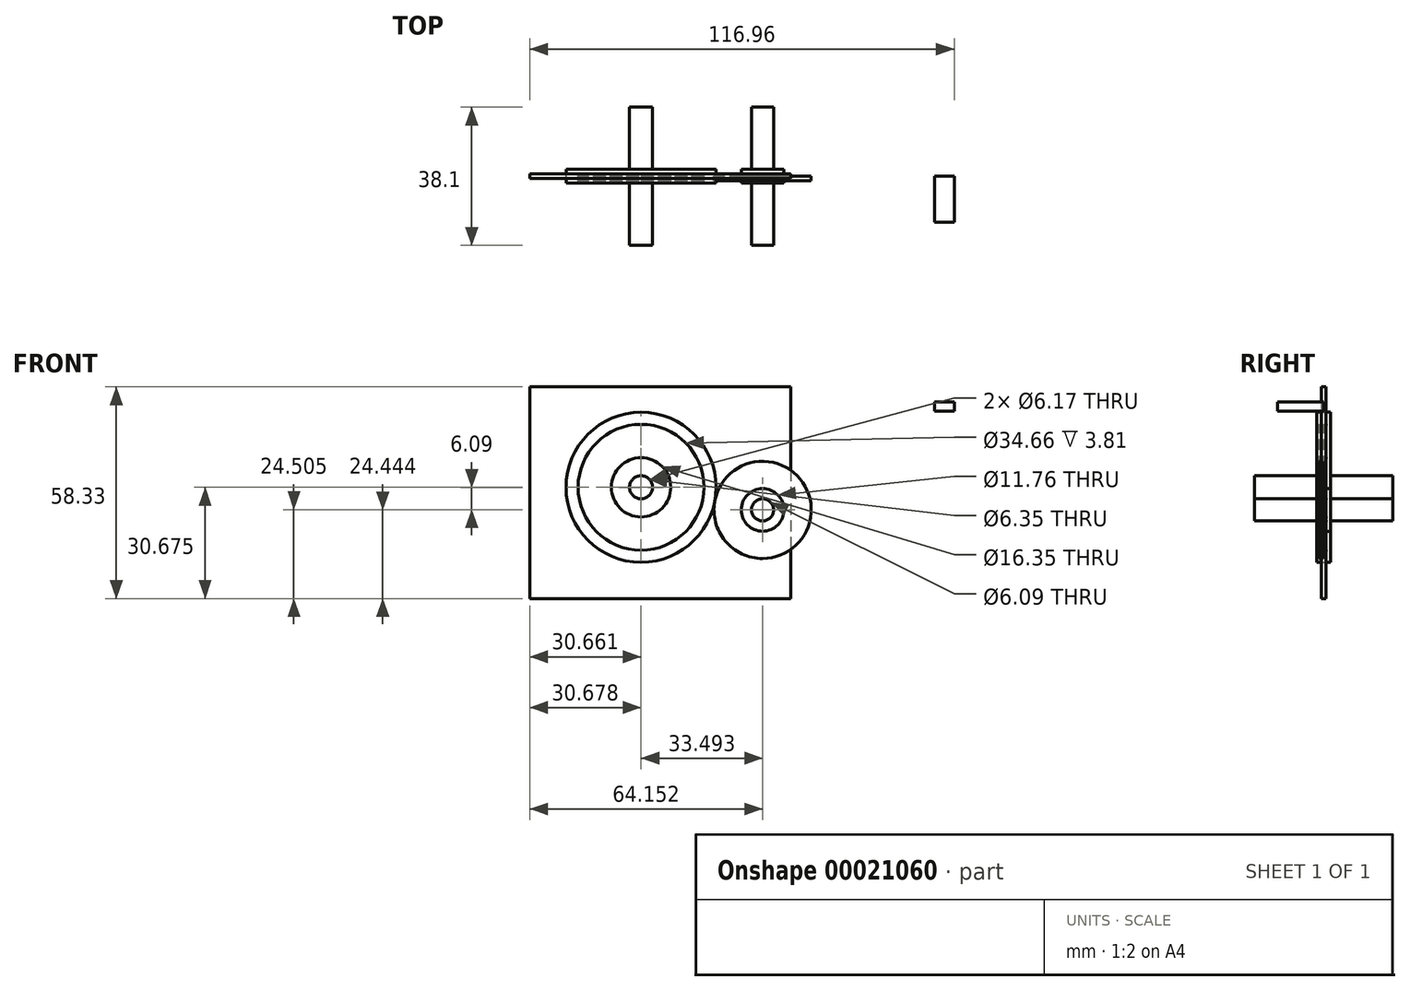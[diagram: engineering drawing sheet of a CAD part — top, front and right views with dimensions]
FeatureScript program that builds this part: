
annotation { "Feature Type Name" : "Feature", "Feature Type Description" : "" }
export const myFeature = defineFeature(function(context is Context, id is Id, definition is map)
    precondition{}
    {
        {
            var Q0;
            Q0=qCreatedBy(makeId("Front.planeOp"),FACE);
            var sketch = newSketch(context, id + "F0", { "sketchPlane" : qUnion([Q0])});
            skCircle(sketch, "E0", {"center": v(13.17, 13.26) * mm, "radius": 13.4 * mm});
            skPoint(sketch, "E0.first.point", {"position": v(11.28, 0) * mm});
            skPoint(sketch, "E0.second.point", {"position": v(0, 15.71) * mm});
            skPoint(sketch, "E0.third.point", {"position": v(25.7, 18.04) * mm});
            skCircle(sketch, "E1", {"center": v(-20.32, 19.5) * mm, "radius": 20.67 * mm});
            skPoint(sketch, "E1.first.point", {"position": v(-13.46, 0) * mm});
            skPoint(sketch, "E1.third.point", {"position": v(-40.92, 17.84) * mm});
            skCircle(sketch, "E2", {"center": v(-20.32, 19.5) * mm, "radius": 17.33 * mm});
            skCircle(sketch, "E3", {"center": v(-20.32, 19.5) * mm, "radius": 8.18 * mm});
            skCircle(sketch, "E4", {"center": v(-20.32, 19.5) * mm, "radius": 3.17 * mm});
            skCircle(sketch, "E5", {"center": v(13.17, 13.26) * mm, "radius": 5.88 * mm});
            skCircle(sketch, "E6", {"center": v(13.17, 13.26) * mm, "radius": 3.05 * mm});
            skLineSegment(sketch, "E7", {"start": v(-19.93, 16.34) * mm, "end": v(-20.32, 19.5) * mm});
            skSolve(sketch);
        }
        {
            var Q0;
            Q0=makeQuery(id+"F0.imprint","IMPRINT",FACE,{"disambiguationData":[TD([[makeQuery(id+"F0.imprint","IMPRINT",EDGE,{"derivedFrom":sQuery(id+"F0.wireOp",EDGE,"E4")}),1.0]])]});
            var Q1;
            Q1=makeQuery(id+"F0.imprint","IMPRINT",FACE,{"disambiguationData":[TD([[makeQuery(id+"F0.imprint","IMPRINT",EDGE,{"derivedFrom":sQuery(id+"F0.wireOp",EDGE,"E6")}),1.0]])]});
            extrude(context, id + "F1", {"entities" : qUnion([Q0, Q1]), "endBound" : BoundingType.SYMMETRIC, "depth" : 38.1 * mm});
        }
        {
            var Q0;
            Q0=makeQuery(id+"F0.imprint","IMPRINT",FACE,{"disambiguationData":[TD([[makeQuery(id+"F0.imprint","IMPRINT",EDGE,{"derivedFrom":sQuery(id+"F0.wireOp",EDGE,"E3")}),1.0]])]});
            var Q1;
            Q1=makeQuery(id+"F0.imprint","IMPRINT",FACE,{"disambiguationData":[TD([[makeQuery(id+"F0.imprint","IMPRINT",EDGE,{"derivedFrom":sQuery(id+"F0.wireOp",EDGE,"E1")}),1.0]])]});
            var Q2;
            Q2=makeQuery(id+"F0.imprint","IMPRINT",FACE,{"disambiguationData":[TD([[makeQuery(id+"F0.imprint","IMPRINT",EDGE,{"derivedFrom":sQuery(id+"F0.wireOp",EDGE,"E5")}),1.0]])]});
            extrude(context, id + "F2", {"entities" : qUnion([Q0, Q1, Q2]), "endBound" : BoundingType.SYMMETRIC, "depth" : 3.8 * mm});
        }
        {
            var Q0;
            Q0=makeQuery(id+"F0.imprint","IMPRINT",FACE,{"disambiguationData":[TD([[makeQuery(id+"F0.imprint","IMPRINT",EDGE,{"derivedFrom":sQuery(id+"F0.wireOp",EDGE,"E2")}),1.0]])]});
            var Q1;
            Q1=makeQuery(id+"F0.imprint","IMPRINT",FACE,{"disambiguationData":[TD([[makeQuery(id+"F0.imprint","IMPRINT",EDGE,{"derivedFrom":sQuery(id+"F0.wireOp",EDGE,"E0")}),1.0]])]});
            extrude(context, id + "F3", {"entities" : qUnion([Q0, Q1]), "depth" : 1.27 * mm});
        }
        {
            var Q0;
            Q0=qCreatedBy(makeId("Front.planeOp"),FACE);
            var sketch = newSketch(context, id + "F4", { "sketchPlane" : qUnion([Q0])});
            skLineSegment(sketch, "E8.bottom", {"start": v(-50.98, 47.15) * mm, "end": v(20.86, 47.15) * mm});
            skLineSegment(sketch, "E8.top", {"start": v(-50.98, -11.18) * mm, "end": v(20.86, -11.18) * mm});
            skLineSegment(sketch, "E8.left", {"start": v(-50.98, 47.15) * mm, "end": v(-50.98, -11.18) * mm});
            skLineSegment(sketch, "E8.right", {"start": v(20.86, 47.15) * mm, "end": v(20.86, -11.18) * mm});
            skCircle(sketch, "E9", {"center": v(-20.3, 19.41) * mm, "radius": 3.09 * mm});
            skPoint(sketch, "E9.first.point", {"position": v(-22.22, 21.84) * mm});
            skPoint(sketch, "E9.second.point", {"position": v(-17.57, 17.97) * mm});
            skPoint(sketch, "E9.third.point", {"position": v(-21.96, 16.8) * mm});
            skCircle(sketch, "E10", {"center": v(13.2, 13.32) * mm, "radius": 3.08 * mm});
            skPoint(sketch, "E10.first.point", {"position": v(10.8, 15.26) * mm});
            skPoint(sketch, "E10.second.point", {"position": v(15.7, 11.52) * mm});
            skPoint(sketch, "E10.third.point", {"position": v(12.34, 10.36) * mm});
            skSolve(sketch);
        }
        {
            var Q0;
            Q0=makeQuery(id+"F4.imprint","IMPRINT",FACE,{"disambiguationData":[TD([[makeQuery(id+"F4.imprint","IMPRINT",EDGE,{"derivedFrom":sQuery(id+"F4.wireOp",EDGE,"E8.bottom")}),-1.0]])]});
            extrude(context, id + "F5", {"entities" : qUnion([Q0]), "endBound" : BoundingType.SYMMETRIC, "depth" : 1.27 * mm});
        }
        {
            var Q0;
            Q0=qCreatedBy(makeId("Front.planeOp"),FACE);
            var sketch = newSketch(context, id + "F6", { "sketchPlane" : qUnion([Q0])});
            skLineSegment(sketch, "E11.bottom", {"start": v(65.98, 43.03) * mm, "end": v(60.5, 43.03) * mm});
            skLineSegment(sketch, "E11.top", {"start": v(65.98, 40.5) * mm, "end": v(60.5, 40.5) * mm});
            skLineSegment(sketch, "E11.left", {"start": v(65.98, 43.03) * mm, "end": v(65.98, 40.5) * mm});
            skLineSegment(sketch, "E11.right", {"start": v(60.5, 43.03) * mm, "end": v(60.5, 40.5) * mm});
            skSolve(sketch);
        }
        {
            var Q0;
            Q0=makeQuery(id+"F6.imprint","IMPRINT",FACE,{"disambiguationData":[TD([[makeQuery(id+"F6.imprint","IMPRINT",EDGE,{"derivedFrom":sQuery(id+"F6.wireOp",EDGE,"E11.bottom")}),1.0]])]});
            extrude(context, id + "F7", {"entities" : qUnion([Q0]), "depth" : 12.7 * mm});
        }
    });
